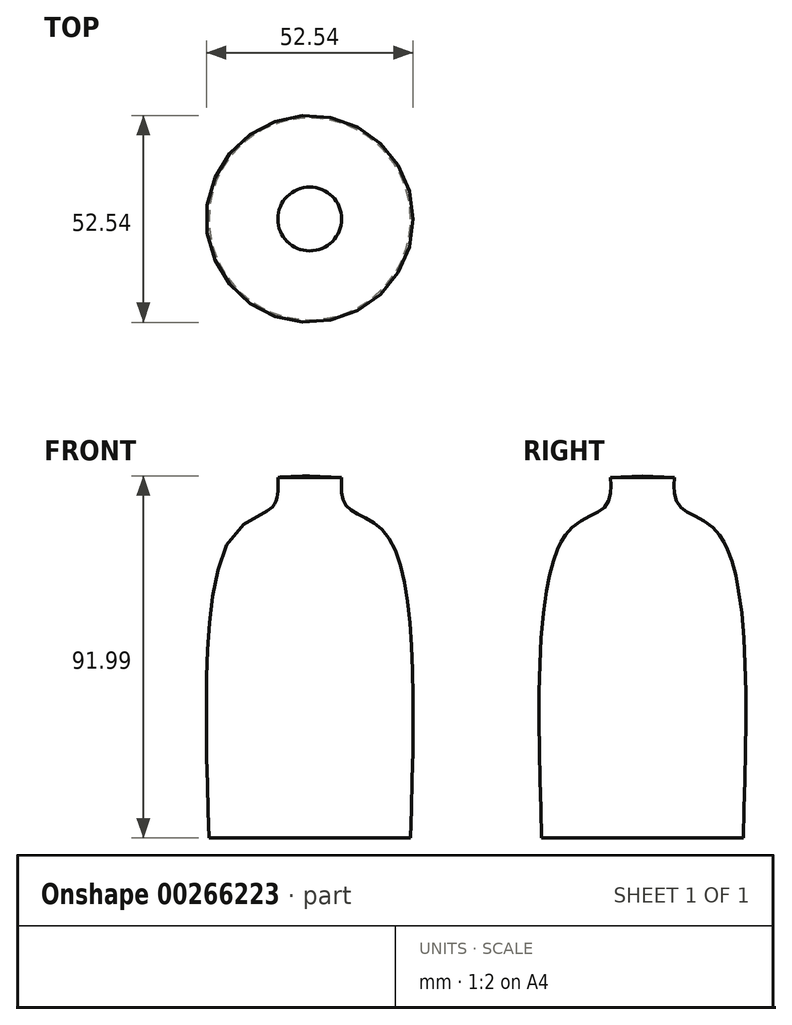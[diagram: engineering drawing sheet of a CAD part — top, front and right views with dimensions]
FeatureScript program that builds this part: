
annotation { "Feature Type Name" : "Feature", "Feature Type Description" : "" }
export const myFeature = defineFeature(function(context is Context, id is Id, definition is map)
    precondition{}
    {
        {
            var Q0;
            Q0=qCreatedBy(makeId("Front.planeOp"),FACE);
            var sketch = newSketch(context, id + "F0", { "sketchPlane" : qUnion([Q0])});
            skFitSpline(sketch, "E0", {"points": [v(-8.11, 55.5) * mm, v(-9.4, 48.12) * mm, v(-19.36, 41.11) * mm, v(-25.63, -36.13) * mm], "startDerivative": vector(2.15, -46.17) * mm, "endDerivative": vector(5.04, -170.87) * mm});
            skLineSegment(sketch, "E1", {"start": v(0, 55.86) * mm, "end": v(0, -37.8) * mm});
            skLineSegment(sketch, "E2", {"start": v(-25.63, -36.13) * mm, "end": v(0, -36.13) * mm});
            skLineSegment(sketch, "E3", {"start": v(-8.11, 55.5) * mm, "end": v(0, 55.86) * mm});
            skSolve(sketch);
        }
        {
            var Q0;
            Q0=makeQuery(id+"F0.imprint","IMPRINT",FACE,{"disambiguationData":[TD([[makeQuery(id+"F0.imprint","IMPRINT",EDGE,{"derivedFrom":sQuery(id+"F0.wireOp",EDGE,"E0")}),1.0]])]});
            var Q1;
            Q1=sQuery(id+"F0.wireOp",EDGE,"E1");
            revolve(context, id + "F1", {"entities" : qUnion([Q0]), "axis" : qUnion([Q1]), "revolveType" : RevolveType.FULL});
        }
    });
